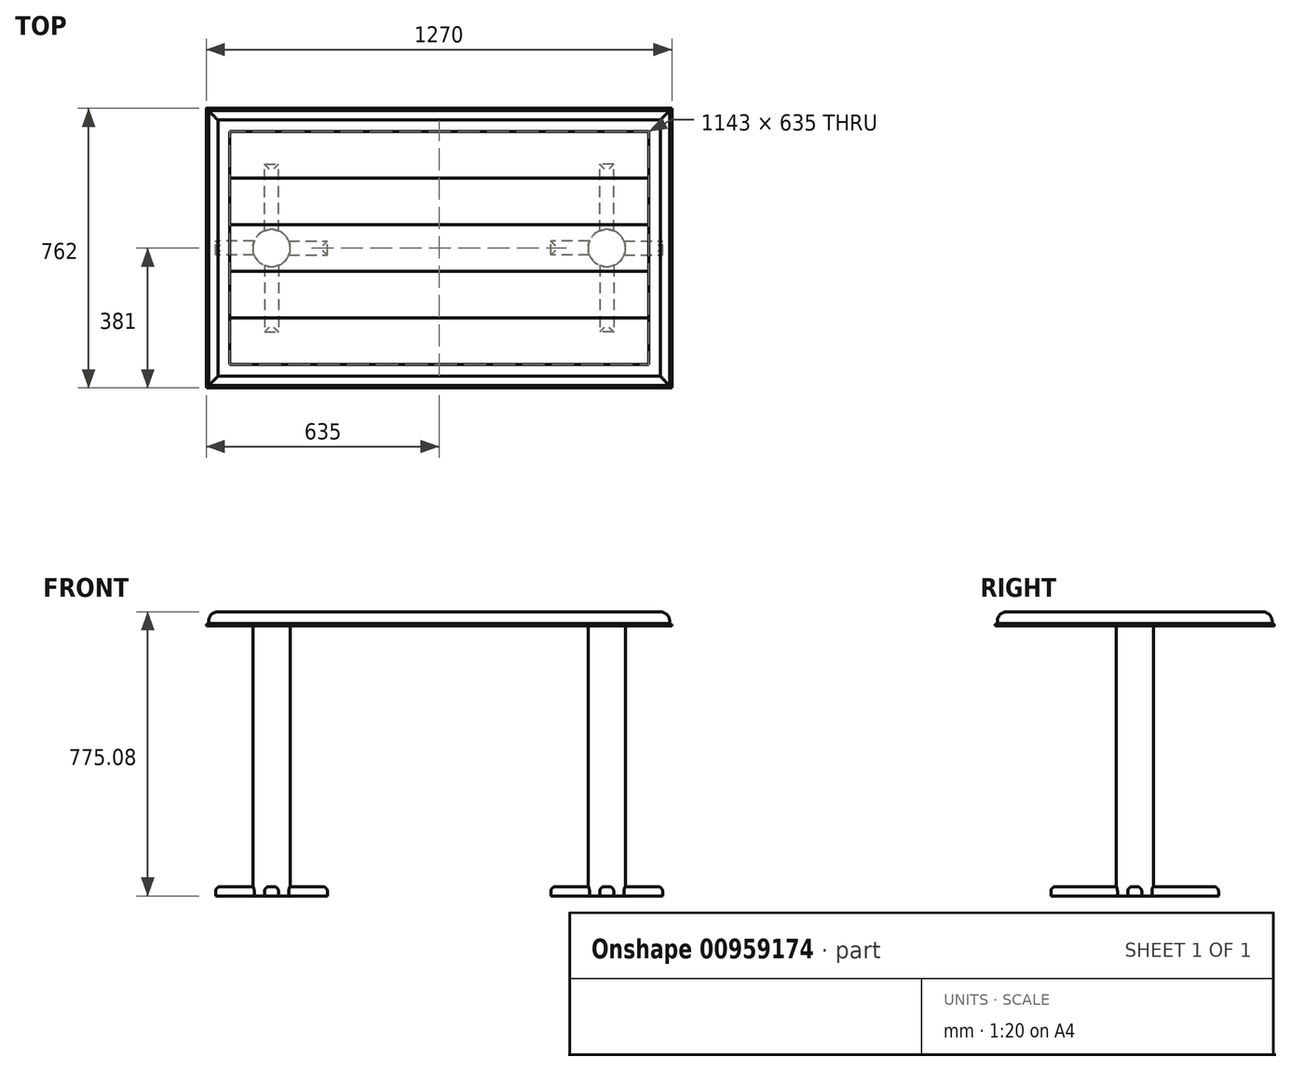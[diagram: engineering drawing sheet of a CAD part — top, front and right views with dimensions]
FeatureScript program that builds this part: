
annotation { "Feature Type Name" : "Feature", "Feature Type Description" : "" }
export const myFeature = defineFeature(function(context is Context, id is Id, definition is map)
    precondition{}
    {
        {
            var Q0;
            Q0=qCreatedBy(makeId("Top.planeOp"),FACE);
            var sketch = newSketch(context, id + "F0", { "sketchPlane" : qUnion([Q0])});
            skPoint(sketch, "E0.middle", {"position": v(0, 0) * mm});
            skPoint(sketch, "E1.visualSharp", {"position": v(-342.9, 342.9) * mm});
            skPoint(sketch, "E2.visualSharp", {"position": v(635, 381) * mm});
            skPoint(sketch, "E3.visualSharp", {"position": v(342.9, -342.9) * mm});
            skPoint(sketch, "E4.visualSharp", {"position": v(-635, -381) * mm});
            skLineSegment(sketch, "E5.bottom", {"start": v(635, 381) * mm, "end": v(-635, 381) * mm});
            skLineSegment(sketch, "E5.top", {"start": v(635, -381) * mm, "end": v(-635, -381) * mm});
            skLineSegment(sketch, "E5.left", {"start": v(635, 381) * mm, "end": v(635, -381) * mm});
            skLineSegment(sketch, "E5.right", {"start": v(-635, 381) * mm, "end": v(-635, -381) * mm});
            skLineSegment(sketch, "E6.0", {"start": v(628.65, 374.65) * mm, "end": v(-628.65, 374.65) * mm});
            skLineSegment(sketch, "E6.1", {"start": v(628.65, 374.65) * mm, "end": v(628.65, -374.65) * mm});
            skLineSegment(sketch, "E6.2", {"start": v(628.65, -374.65) * mm, "end": v(-628.65, -374.65) * mm});
            skLineSegment(sketch, "E6.3", {"start": v(-628.65, 374.65) * mm, "end": v(-628.65, -374.65) * mm});
            skSolve(sketch);
        }
        {
            var Q0;
            Q0=qSketchRegion(id+"F0",true);
            extrude(context, id + "F1", {"entities" : qUnion([Q0]), "depth" : 6.35 * mm, "offsetDistance" : 25.4 * mm});
        }
        {
            var Q0;
            Q0=makeQuery(id+"F0.imprint","IMPRINT",FACE,{"disambiguationData":[TD([[makeQuery(id+"F0.imprint","IMPRINT",EDGE,{"derivedFrom":sQuery(id+"F0.wireOp",EDGE,"E6.0")}),1.0]])]});
            var sketch = newSketch(context, id + "F2", { "sketchPlane" : qUnion([Q0])});
            skSolve(sketch);
        }
        {
            var Q0;
            Q0=makeQuery(id+"F2.imprint","IMPRINT",FACE,{"disambiguationData":[TD([[makeQuery(id+"F2.imprint","IMPRINT",EDGE,{"derivedFrom":sQuery(id+"F2.wireOp",EDGE,"7v3jKXoN-9Vkt-3N5j-tcrE-iFcyYjooLoXS")}),-1.0]])]});
            var Q1;
            Q1=makeQuery(id+"F0.imprint","IMPRINT",FACE,{"disambiguationData":[TD([[makeQuery(id+"F0.imprint","IMPRINT",EDGE,{"derivedFrom":sQuery(id+"F0.wireOp",EDGE,"E6.0")}),1.0]])]});
            extrude(context, id + "F3", {"entities" : qUnion([Q0, Q1]), "operationType" : NewBodyOperationType.ADD, "depth" : 38.1 * mm, "offsetDistance" : 25.4 * mm});
        }
        {
            var Q0;
            Q0=makeQuery(id+"F3.opExtrude","CAP_EDGE",EDGE,{"disambiguationData":[OSD([sQuery(id+"F0.wireOp",EDGE,"E6.0")])],"isStart":false});
            var Q1;
            Q1=makeQuery(id+"F3.opExtrude","CAP_EDGE",EDGE,{"disambiguationData":[OSD([sQuery(id+"F0.wireOp",EDGE,"E6.3")])],"isStart":false});
            var Q2;
            Q2=makeQuery(id+"F3.opExtrude","CAP_EDGE",EDGE,{"disambiguationData":[OSD([sQuery(id+"F0.wireOp",EDGE,"E6.2")])],"isStart":false});
            var Q3;
            Q3=makeQuery(id+"F3.opExtrude","CAP_EDGE",EDGE,{"disambiguationData":[OSD([sQuery(id+"F0.wireOp",EDGE,"E6.1")])],"isStart":false});
            fillet(context, id + "F4", {"entities" : qUnion([Q0, Q1, Q2, Q3]), "radius" : 25.4 * mm, "tangentPropagation" : true, "allowEdgeOverflow" : false});
        }
        {
            var Q0;
            Q0=makeQuery(id+"F1.opExtrude","CAP_EDGE",EDGE,{"disambiguationData":[OSD([sQuery(id+"F0.wireOp",EDGE,"E5.right")])],"isStart":false});
            var Q1;
            Q1=makeQuery(id+"F1.opExtrude","CAP_EDGE",EDGE,{"disambiguationData":[OSD([sQuery(id+"F0.wireOp",EDGE,"E5.top")])],"isStart":false});
            var Q2;
            Q2=makeQuery(id+"F1.opExtrude","CAP_EDGE",EDGE,{"disambiguationData":[OSD([sQuery(id+"F0.wireOp",EDGE,"E5.left")])],"isStart":false});
            var Q3;
            Q3=makeQuery(id+"F1.opExtrude","CAP_EDGE",EDGE,{"disambiguationData":[OSD([sQuery(id+"F0.wireOp",EDGE,"E5.bottom")])],"isStart":false});
            fillet(context, id + "F5", {"entities" : qUnion([Q0, Q1, Q2, Q3]), "radius" : 6.35 * mm, "tangentPropagation" : true, "allowEdgeOverflow" : false});
        }
        {
            var Q0;
            Q0=qCreatedBy(makeId("Top.planeOp"),FACE);
            var sketch = newSketch(context, id + "F6", { "sketchPlane" : qUnion([Q0])});
            skLineSegment(sketch, "E7", {"start": v(0, 541.66) * mm, "end": v(0, -673.96) * mm, "construction": true});
            skLineSegment(sketch, "E8", {"start": v(457.2, 0) * mm, "end": v(-457.2, 0) * mm, "construction": true});
            skCircle(sketch, "E9", {"center": v(457.2, 0) * mm, "radius": 50.8 * mm});
            skCircle(sketch, "E10", {"center": v(-457.2, 0) * mm, "radius": 50.8 * mm});
            skSolve(sketch);
        }
        {
            var Q0;
            Q0=qSketchRegion(id+"F6",true);
            extrude(context, id + "F7", {"entities" : qUnion([Q0]), "operationType" : NewBodyOperationType.ADD, "oppositeDirection" : true, "depth" : 736.6 * mm, "offsetDistance" : 25.4 * mm});
        }
        {
            var Q0;
            Q0=makeQuery(id+"F7.opExtrude","CAP_FACE",FACE,{"disambiguationData":[OSD([sQuery(id+"F6.wireOp",EDGE,"E9")])],"isStart":false});
            var sketch = newSketch(context, id + "F8", { "sketchPlane" : qUnion([Q0])});
            skCircle(sketch, "E11.0", {"center": v(-457.2, 0) * mm, "radius": 50.8 * mm, "construction": true});
            skCircle(sketch, "E12.0", {"center": v(457.2, 0) * mm, "radius": 50.8 * mm, "construction": true});
            skLineSegment(sketch, "E13", {"start": v(-457.2, 0) * mm, "end": v(-457.2, 228.6) * mm, "construction": true});
            skLineSegment(sketch, "E14.0", {"start": v(-438.15, 19.05) * mm, "end": v(-438.15, 228.6) * mm});
            skLineSegment(sketch, "E15.0", {"start": v(-476.25, 19.05) * mm, "end": v(-476.25, 228.6) * mm});
            skLineSegment(sketch, "E16.0", {"start": v(622.3, -368.3) * mm, "end": v(-622.3, -368.3) * mm});
            skLineSegment(sketch, "E16.1", {"start": v(622.3, 368.3) * mm, "end": v(622.3, -368.3) * mm});
            skLineSegment(sketch, "E16.2", {"start": v(-622.3, 368.3) * mm, "end": v(622.3, 368.3) * mm});
            skLineSegment(sketch, "E16.3", {"start": v(-622.3, -368.3) * mm, "end": v(-622.3, 368.3) * mm});
            skLineSegment(sketch, "E17", {"start": v(-476.25, 228.6) * mm, "end": v(-438.15, 228.6) * mm});
            skLineSegment(sketch, "E18", {"start": v(-476.25, 0) * mm, "end": v(-438.15, 0) * mm});
            skLineSegment(sketch, "E19", {"start": v(-781.95, 0) * mm, "end": v(-457.2, 0) * mm, "construction": true});
            skLineSegment(sketch, "E20", {"start": v(0, 485.08) * mm, "end": v(0, -541.24) * mm, "construction": true});
            skLineSegment(sketch, "E21.MirrorCS", {"start": v(-438.15, -19.05) * mm, "end": v(-438.15, -228.6) * mm});
            skLineSegment(sketch, "E22.MirrorCS", {"start": v(-476.25, -228.6) * mm, "end": v(-438.15, -228.6) * mm});
            skLineSegment(sketch, "E23.MirrorCS", {"start": v(-476.25, -19.05) * mm, "end": v(-476.25, -228.6) * mm});
            skLineSegment(sketch, "E24", {"start": v(-476.25, 0) * mm, "end": v(-609.6, 0) * mm, "construction": true});
            skLineSegment(sketch, "E25.0", {"start": v(-476.25, 19.05) * mm, "end": v(-609.6, 19.05) * mm});
            skLineSegment(sketch, "E26.0", {"start": v(-476.25, -19.05) * mm, "end": v(-609.6, -19.05) * mm});
            skLineSegment(sketch, "E27", {"start": v(-609.6, 19.05) * mm, "end": v(-609.6, -19.05) * mm});
            skLineSegment(sketch, "E28.MirrorCS", {"start": v(-438.15, 19.05) * mm, "end": v(-304.8, 19.05) * mm});
            skLineSegment(sketch, "E29.MirrorCS", {"start": v(-304.8, 19.05) * mm, "end": v(-304.8, -19.05) * mm});
            skLineSegment(sketch, "E30.MirrorCS", {"start": v(-438.15, -19.05) * mm, "end": v(-304.8, -19.05) * mm});
            skLineSegment(sketch, "E31.MirrorCS", {"start": v(457.2, 19.05) * mm, "end": v(304.8, 19.05) * mm});
            skPoint(sketch, "E32.orphan", {"position": v(-457.2, 19.05) * mm});
            skLineSegment(sketch, "E33.trimOffspring", {"start": v(-438.15, 0) * mm, "end": v(760.65, 0) * mm, "construction": true});
            skPoint(sketch, "E34.orphan", {"position": v(-457.2, -19.05) * mm});
            skPoint(sketch, "E35.orphan", {"position": v(-438.15, 0) * mm});
            skSolve(sketch);
        }
        {
            var Q0;
            Q0=makeQuery(id+"F8.imprint","IMPRINT",FACE,{"disambiguationData":[TD([[makeQuery(id+"F8.imprint","IMPRINT",EDGE,{"derivedFrom":sQuery(id+"F8.wireOp",EDGE,"E14.0")}),1.0]])]});
            extrude(context, id + "F9", {"entities" : qUnion([Q0]), "oppositeDirection" : true, "depth" : 25.4 * mm, "offsetDistance" : 25.4 * mm});
        }
        {
            var Q0;
            {var subQ0=sQuery(id+"F8.wireOp",EDGE,"E26.0");var subQ1=sQuery(id+"F8.wireOp",EDGE,"E25.0");var subQ2=sQuery(id+"F8.wireOp",EDGE,"E27");Q0=makeQuery(id+"F9.boolean.opBoolean","SPLIT",FACE,{"disambiguationData":[TD([makeQuery(id+"F9.opExtrude","SWEPT_FACE",FACE,{"disambiguationData":[OSD([subQ1])]})])],"derivedFrom":makeQuery(id+"F9.opExtrude","CAP_FACE",FACE,{"disambiguationData":[OSD([sQuery(id+"F8.wireOp",EDGE,"E14.0"),sQuery(id+"F8.wireOp",EDGE,"E15.0"),sQuery(id+"F8.wireOp",EDGE,"E17"),sQuery(id+"F8.wireOp",EDGE,"E21.MirrorCS"),sQuery(id+"F8.wireOp",EDGE,"E22.MirrorCS"),sQuery(id+"F8.wireOp",EDGE,"E23.MirrorCS"),subQ1,subQ0,subQ2,sQuery(id+"F8.wireOp",EDGE,"E28.MirrorCS"),sQuery(id+"F8.wireOp",EDGE,"E29.MirrorCS"),sQuery(id+"F8.wireOp",EDGE,"E30.MirrorCS")])],"isStart":false})});}
            var Q1;
            {var subQ0=sQuery(id+"F8.wireOp",EDGE,"E17");var subQ1=sQuery(id+"F8.wireOp",EDGE,"E14.0");var subQ2=sQuery(id+"F8.wireOp",EDGE,"E15.0");Q1=makeQuery(id+"F9.boolean.opBoolean","SPLIT",FACE,{"disambiguationData":[TD([makeQuery(id+"F9.opExtrude","SWEPT_FACE",FACE,{"disambiguationData":[OSD([subQ1])]})])],"derivedFrom":makeQuery(id+"F9.opExtrude","CAP_FACE",FACE,{"disambiguationData":[OSD([subQ1,subQ2,subQ0,sQuery(id+"F8.wireOp",EDGE,"E21.MirrorCS"),sQuery(id+"F8.wireOp",EDGE,"E22.MirrorCS"),sQuery(id+"F8.wireOp",EDGE,"E23.MirrorCS"),sQuery(id+"F8.wireOp",EDGE,"E25.0"),sQuery(id+"F8.wireOp",EDGE,"E26.0"),sQuery(id+"F8.wireOp",EDGE,"E27"),sQuery(id+"F8.wireOp",EDGE,"E28.MirrorCS"),sQuery(id+"F8.wireOp",EDGE,"E29.MirrorCS"),sQuery(id+"F8.wireOp",EDGE,"E30.MirrorCS")])],"isStart":false})});}
            var Q2;
            {var subQ0=sQuery(id+"F8.wireOp",EDGE,"E28.MirrorCS");var subQ1=sQuery(id+"F8.wireOp",EDGE,"E29.MirrorCS");var subQ2=sQuery(id+"F8.wireOp",EDGE,"E30.MirrorCS");Q2=makeQuery(id+"F9.boolean.opBoolean","SPLIT",FACE,{"disambiguationData":[TD([makeQuery(id+"F9.opExtrude","SWEPT_FACE",FACE,{"disambiguationData":[OSD([subQ0])]})])],"derivedFrom":makeQuery(id+"F9.opExtrude","CAP_FACE",FACE,{"disambiguationData":[OSD([sQuery(id+"F8.wireOp",EDGE,"E14.0"),sQuery(id+"F8.wireOp",EDGE,"E15.0"),sQuery(id+"F8.wireOp",EDGE,"E17"),sQuery(id+"F8.wireOp",EDGE,"E21.MirrorCS"),sQuery(id+"F8.wireOp",EDGE,"E22.MirrorCS"),sQuery(id+"F8.wireOp",EDGE,"E23.MirrorCS"),sQuery(id+"F8.wireOp",EDGE,"E25.0"),sQuery(id+"F8.wireOp",EDGE,"E26.0"),sQuery(id+"F8.wireOp",EDGE,"E27"),subQ0,subQ1,subQ2])],"isStart":false})});}
            var Q3;
            {var subQ0=sQuery(id+"F8.wireOp",EDGE,"E21.MirrorCS");var subQ1=sQuery(id+"F8.wireOp",EDGE,"E22.MirrorCS");var subQ2=sQuery(id+"F8.wireOp",EDGE,"E23.MirrorCS");Q3=makeQuery(id+"F9.boolean.opBoolean","SPLIT",FACE,{"disambiguationData":[TD([makeQuery(id+"F9.opExtrude","SWEPT_FACE",FACE,{"disambiguationData":[OSD([subQ0])]})])],"derivedFrom":makeQuery(id+"F9.opExtrude","CAP_FACE",FACE,{"disambiguationData":[OSD([sQuery(id+"F8.wireOp",EDGE,"E14.0"),sQuery(id+"F8.wireOp",EDGE,"E15.0"),sQuery(id+"F8.wireOp",EDGE,"E17"),subQ0,subQ1,subQ2,sQuery(id+"F8.wireOp",EDGE,"E25.0"),sQuery(id+"F8.wireOp",EDGE,"E26.0"),sQuery(id+"F8.wireOp",EDGE,"E27"),sQuery(id+"F8.wireOp",EDGE,"E28.MirrorCS"),sQuery(id+"F8.wireOp",EDGE,"E29.MirrorCS"),sQuery(id+"F8.wireOp",EDGE,"E30.MirrorCS")])],"isStart":false})});}
            fillet(context, id + "F10", {"entities" : qUnion([Q0, Q1, Q2, Q3]), "radius" : 12.7 * mm, "tangentPropagation" : true, "allowEdgeOverflow" : false});
        }
        {
            var Q0;
            Q0=makeQuery(id+"F9.opExtrude","SWEPT_BODY",BODY,{"disambiguationData":[OSD([sQuery(id+"F8.wireOp",EDGE,"E14.0"),sQuery(id+"F8.wireOp",EDGE,"E15.0"),sQuery(id+"F8.wireOp",EDGE,"E17"),sQuery(id+"F8.wireOp",EDGE,"E21.MirrorCS"),sQuery(id+"F8.wireOp",EDGE,"E22.MirrorCS"),sQuery(id+"F8.wireOp",EDGE,"E23.MirrorCS"),sQuery(id+"F8.wireOp",EDGE,"E25.0"),sQuery(id+"F8.wireOp",EDGE,"E26.0"),sQuery(id+"F8.wireOp",EDGE,"E27"),sQuery(id+"F8.wireOp",EDGE,"E28.MirrorCS"),sQuery(id+"F8.wireOp",EDGE,"E29.MirrorCS"),sQuery(id+"F8.wireOp",EDGE,"E30.MirrorCS")])]});
            var Q1;
            Q1=qCreatedBy(makeId("Right.planeOp"),FACE);
            mirror(context, id + "F11", {"operationType" : NewBodyOperationType.ADD, "entities" : qUnion([Q0]), "mirrorPlane" : qUnion([Q1])});
        }
        {
            var Q0;
            Q0=makeQuery(id+"F3.opExtrude","CAP_FACE",FACE,{"disambiguationData":[OSD([sQuery(id+"F0.wireOp",EDGE,"E6.0"),sQuery(id+"F0.wireOp",EDGE,"E6.1"),sQuery(id+"F0.wireOp",EDGE,"E6.2"),sQuery(id+"F0.wireOp",EDGE,"E6.3")])],"isStart":false});
            var sketch = newSketch(context, id + "F12", { "sketchPlane" : qUnion([Q0])});
            skLineSegment(sketch, "E36.0", {"start": v(571.5, 317.5) * mm, "end": v(-571.5, 317.5) * mm});
            skLineSegment(sketch, "E36.1", {"start": v(571.5, 317.5) * mm, "end": v(571.5, -317.5) * mm});
            skLineSegment(sketch, "E36.2", {"start": v(571.5, -317.5) * mm, "end": v(-571.5, -317.5) * mm});
            skLineSegment(sketch, "E36.3", {"start": v(-571.5, 317.5) * mm, "end": v(-571.5, -317.5) * mm});
            skLineSegment(sketch, "E37.0", {"start": v(-609.6, 355.6) * mm, "end": v(-609.6, -355.6) * mm});
            skLineSegment(sketch, "E37.1", {"start": v(609.6, 355.6) * mm, "end": v(-609.6, 355.6) * mm});
            skLineSegment(sketch, "E37.2", {"start": v(609.6, -355.6) * mm, "end": v(609.6, 355.6) * mm});
            skLineSegment(sketch, "E37.3", {"start": v(-609.6, -355.6) * mm, "end": v(609.6, -355.6) * mm});
            skLineSegment(sketch, "E38.direction1", {"start": v(-444.5, -317.5) * mm, "end": v(-444.5, -317.5) * mm});
            skLineSegment(sketch, "E39", {"start": v(-571.5, 190.5) * mm, "end": v(571.5, 190.5) * mm});
            skLineSegment(sketch, "E40", {"start": v(-571.5, 63.5) * mm, "end": v(571.5, 63.5) * mm});
            skLineSegment(sketch, "E41", {"start": v(-571.5, -63.5) * mm, "end": v(571.5, -63.5) * mm});
            skLineSegment(sketch, "E42", {"start": v(-571.5, -190.5) * mm, "end": v(571.5, -190.5) * mm});
            skSolve(sketch);
        }
        {
            var Q0;
            {var subQ0=sQuery(id+"F12.wireOp",EDGE,"E36.3");Q0=makeQuery(id+"F12.imprint","IMPRINT",FACE,{"disambiguationData":[TD([[makeQuery(id+"F12.imprint","IMPRINT",EDGE,{"derivedFrom":subQ0}),-1.0]])]});}
            extrude(context, id + "F13", {"entities" : qUnion([Q0]), "depth" : 0.38 * mm, "offsetDistance" : 25.4 * mm});
        }
        {
            var Q0;
            {var subQ0=sQuery(id+"F12.wireOp",EDGE,"E36.0");Q0=makeQuery(id+"F12.imprint","IMPRINT",FACE,{"disambiguationData":[TD([[makeQuery(id+"F12.imprint","IMPRINT",EDGE,{"derivedFrom":subQ0}),1.0]])]});}
            var Q1;
            {var subQ0=sQuery(id+"F12.wireOp",EDGE,"E40");Q1=makeQuery(id+"F12.imprint","IMPRINT",FACE,{"disambiguationData":[TD([[makeQuery(id+"F12.imprint","IMPRINT",EDGE,{"derivedFrom":subQ0}),-1.0]])]});}
            var Q2;
            {var subQ0=sQuery(id+"F12.wireOp",EDGE,"E36.2");Q2=makeQuery(id+"F12.imprint","IMPRINT",FACE,{"disambiguationData":[TD([[makeQuery(id+"F12.imprint","IMPRINT",EDGE,{"derivedFrom":subQ0}),-1.0]])]});}
            extrude(context, id + "F14", {"entities" : qUnion([Q0, Q1, Q2]), "depth" : 0.32 * mm, "offsetDistance" : 25.4 * mm});
        }
    });
